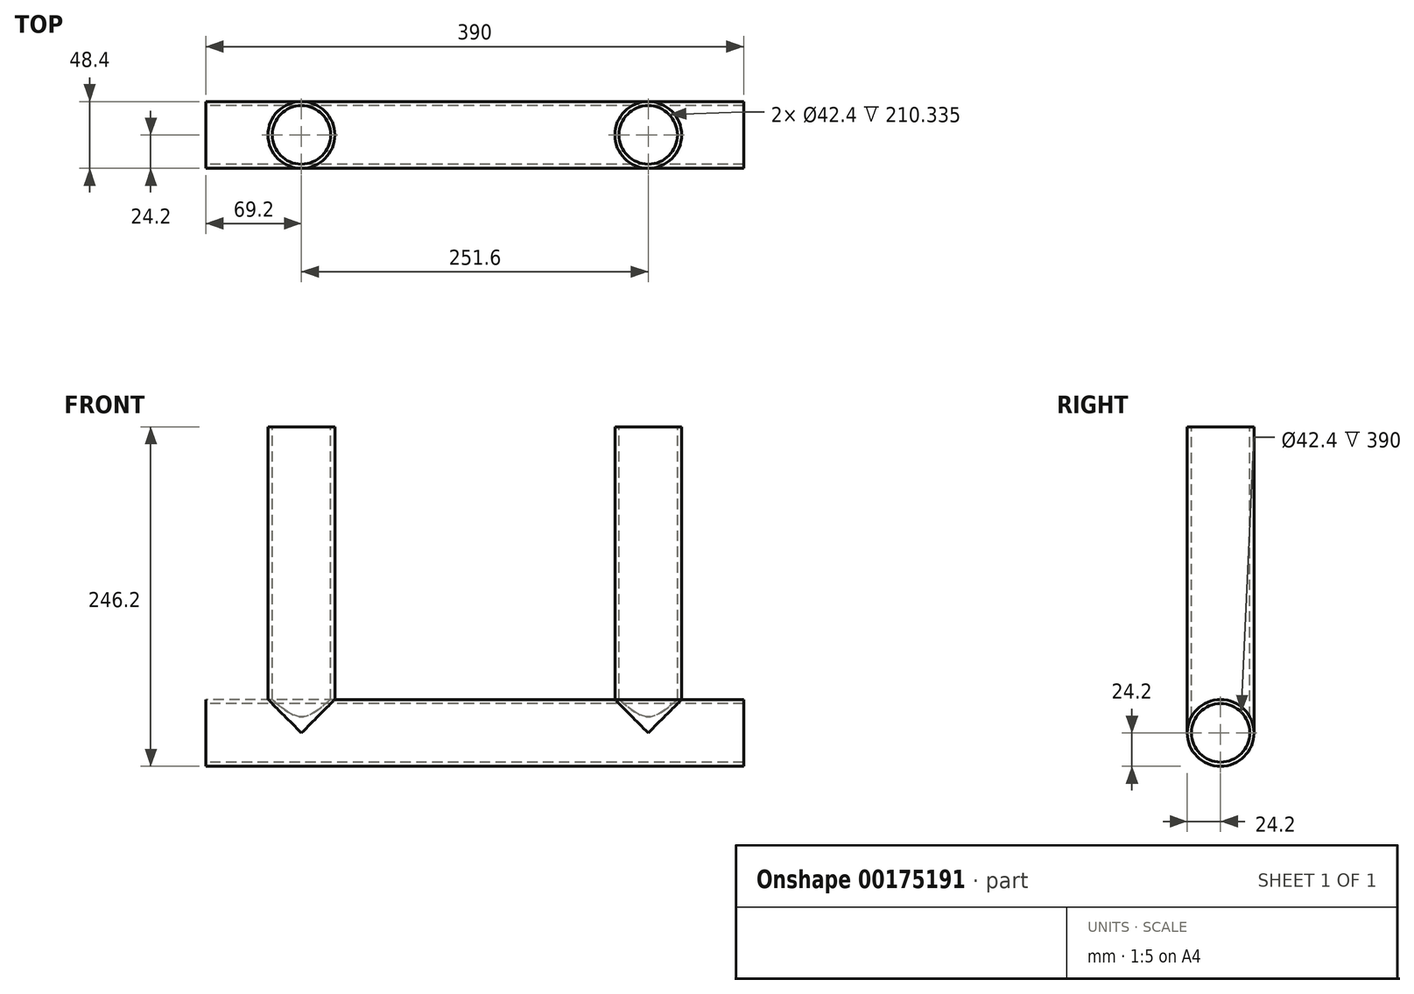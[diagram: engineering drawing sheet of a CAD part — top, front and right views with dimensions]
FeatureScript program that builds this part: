
annotation { "Feature Type Name" : "Feature", "Feature Type Description" : "" }
export const myFeature = defineFeature(function(context is Context, id is Id, definition is map)
    precondition{}
    {
        {
            var Q0;
            Q0=qCreatedBy(makeId("Right.planeOp"),FACE);
            var sketch = newSketch(context, id + "F0", { "sketchPlane" : qUnion([Q0])});
            skCircle(sketch, "E0", {"center": v(0, 0) * mm, "radius": 24.2 * mm});
            skCircle(sketch, "E1.0", {"center": v(0, 0) * mm, "radius": 21.2 * mm});
            skSolve(sketch);
        }
        {
            var Q0;
            Q0 = qSketchRegion(id + "F0", true);
            extrude(context, id + "F1", {"entities" : qUnion([Q0]), "endBound" : BoundingType.SYMMETRIC, "depth" : 390 * mm});
        }
        {
            var Q0;
            Q0=qCreatedBy(makeId("Top.planeOp"),FACE);
            cPlane(context, id + "F2", {"entities" : qUnion([Q0]), "cplaneType" : CPlaneType.OFFSET, "offset" : 222 * mm, "width" : 150 * mm, "height" : 150 * mm});
        }
        {
            var Q0;
            Q0=qCreatedBy(id+"F2.planeOp",FACE);
            var sketch = newSketch(context, id + "F3", { "sketchPlane" : qUnion([Q0])});
            skCircle(sketch, "E2", {"center": v(-125.8, 0) * mm, "radius": 24.2 * mm});
            skCircle(sketch, "E3.0", {"center": v(-125.8, 0) * mm, "radius": 21.2 * mm});
            skCircle(sketch, "E4.MirrorC", {"center": v(125.8, 0) * mm, "radius": 24.2 * mm});
            skCircle(sketch, "E5.MirrorC", {"center": v(125.8, 0) * mm, "radius": 21.2 * mm});
            skSolve(sketch);
        }
        {
            var Q0;
            Q0 = qSketchRegion(id + "F3", true);
            extrude(context, id + "F4", {"entities" : qUnion([Q0]), "endBound" : BoundingType.UP_TO_NEXT, "oppositeDirection" : true, "depth" : 25 * mm});
        }
    });
